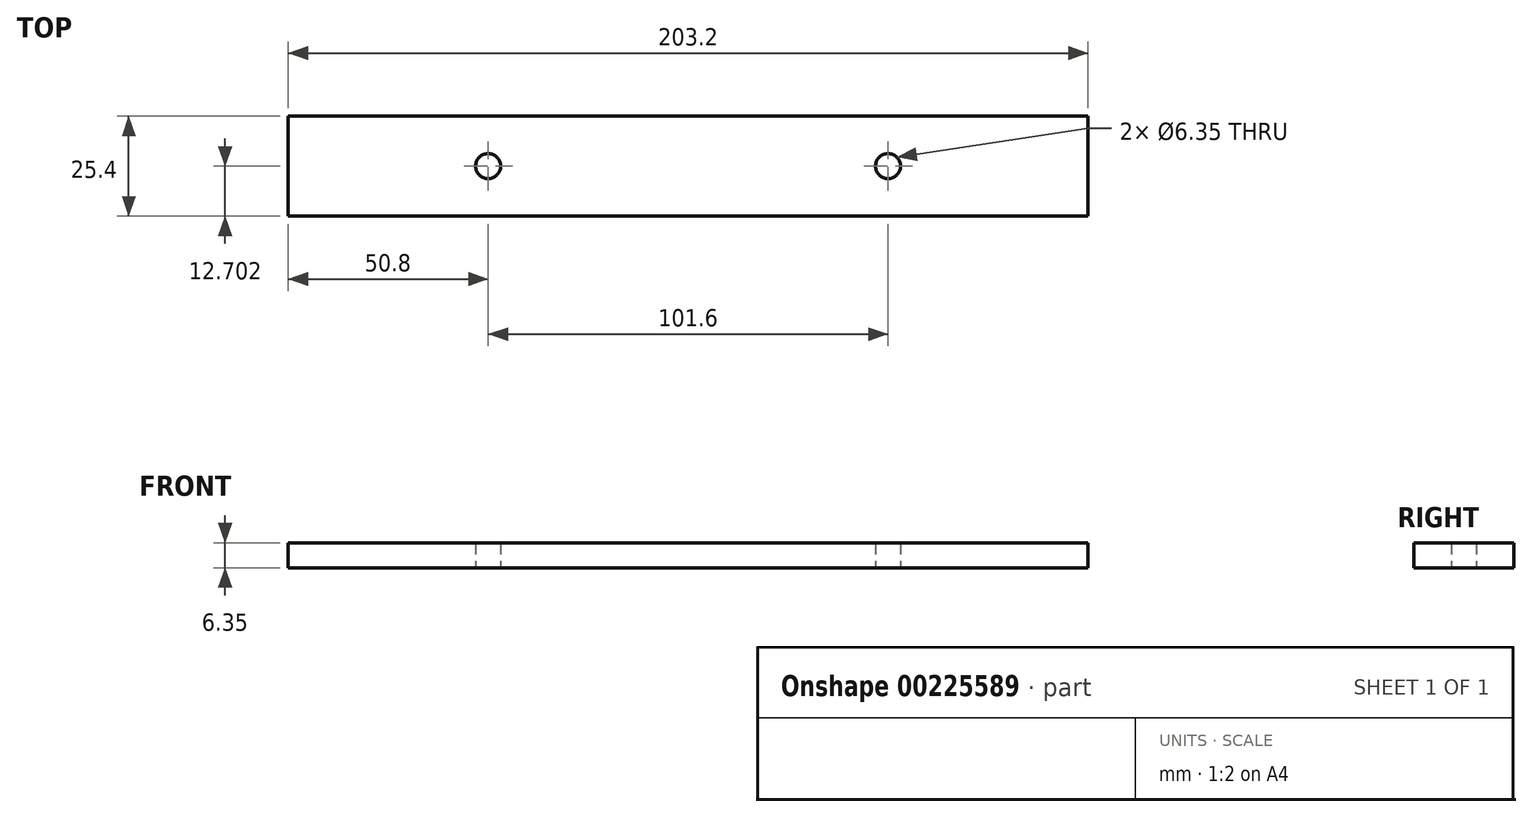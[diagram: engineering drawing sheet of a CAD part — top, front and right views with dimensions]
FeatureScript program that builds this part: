
annotation { "Feature Type Name" : "Feature", "Feature Type Description" : "" }
export const myFeature = defineFeature(function(context is Context, id is Id, definition is map)
    precondition{}
    {
        {
            var Q0;
            Q0=qCreatedBy(makeId("Top.planeOp"),FACE);
            var sketch = newSketch(context, id + "F0", { "sketchPlane" : qUnion([Q0])});
            skLineSegment(sketch, "E0.bottom", {"start": v(76.2, -116.74) * mm, "end": v(-76.2, -116.74) * mm});
            skLineSegment(sketch, "E0.top", {"start": v(76.2, 116.74) * mm, "end": v(-76.2, 116.74) * mm});
            skLineSegment(sketch, "E0.left", {"start": v(76.2, -116.74) * mm, "end": v(76.2, 116.74) * mm});
            skLineSegment(sketch, "E0.right", {"start": v(-76.2, -116.74) * mm, "end": v(-76.2, 116.74) * mm});
            skPoint(sketch, "E0.middle", {"position": v(0, 0) * mm});
            skLineSegment(sketch, "E1.0", {"start": v(101.6, 142.14) * mm, "end": v(-101.6, 142.14) * mm});
            skLineSegment(sketch, "E1.1", {"start": v(101.6, -142.14) * mm, "end": v(101.6, 142.14) * mm});
            skLineSegment(sketch, "E1.2", {"start": v(101.6, -142.14) * mm, "end": v(-101.6, -142.14) * mm});
            skLineSegment(sketch, "E1.3", {"start": v(-101.6, -142.14) * mm, "end": v(-101.6, -116.74) * mm});
            skLineSegment(sketch, "E2", {"start": v(-76.2, 116.74) * mm, "end": v(-101.6, 116.74) * mm});
            skLineSegment(sketch, "E3", {"start": v(-76.2, -116.74) * mm, "end": v(-101.6, -116.74) * mm});
            skLineSegment(sketch, "E4.trimOffspring", {"start": v(-101.6, 116.74) * mm, "end": v(-101.6, 142.14) * mm});
            skLineSegment(sketch, "E5", {"start": v(76.2, 116.74) * mm, "end": v(101.6, 116.74) * mm});
            skLineSegment(sketch, "E6", {"start": v(76.2, -116.74) * mm, "end": v(101.6, -116.74) * mm});
            skLineSegment(sketch, "E7", {"start": v(88.9, 116.74) * mm, "end": v(88.9, -116.74) * mm});
            skCircle(sketch, "E8", {"center": v(-50.8, -129.44) * mm, "radius": 3.18 * mm});
            skPoint(sketch, "E8.centerSnap0", {"position": v(-101.6, -129.44) * mm});
            skCircle(sketch, "E9", {"center": v(50.8, -129.44) * mm, "radius": 3.18 * mm});
            skSolve(sketch);
        }
        {
            var Q0;
            Q0=makeQuery(id+"F0.imprint","IMPRINT",FACE,{"disambiguationData":[TD([[makeQuery(id+"F0.imprint","IMPRINT",EDGE,{"derivedFrom":sQuery(id+"F0.wireOp",EDGE,"E0.bottom")}),1.0]])]});
            var Q1;
            {var subQ0=sQuery(id+"F0.wireOp",EDGE,"SyIENNwF-CHkI-if3g-Oxzw-q1lJXSxW9fIR");Q1=makeQuery(id+"F0.imprint","IMPRINT",FACE,{"disambiguationData":[TD([[makeQuery(id+"F0.imprint","IMPRINT",EDGE,{"derivedFrom":subQ0}),-1.0]])]});}
            extrude(context, id + "F1", {"entities" : qUnion([Q0, Q1]), "depth" : 6.35 * mm});
        }
    });
